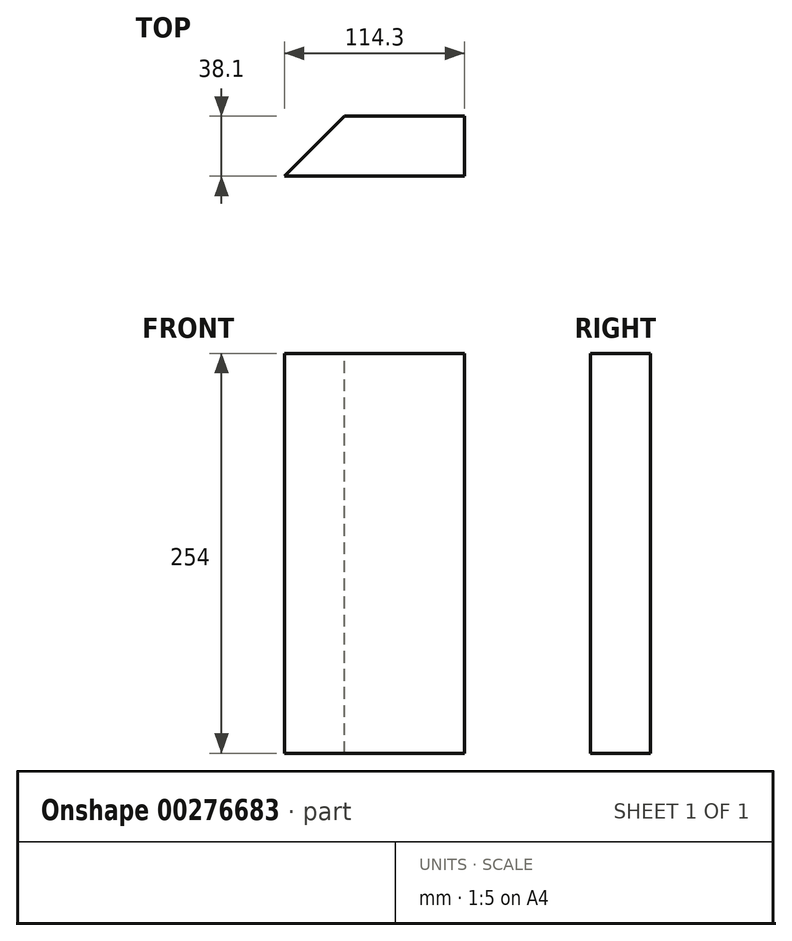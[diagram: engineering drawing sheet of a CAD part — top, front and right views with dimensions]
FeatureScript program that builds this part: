
annotation { "Feature Type Name" : "Feature", "Feature Type Description" : "" }
export const myFeature = defineFeature(function(context is Context, id is Id, definition is map)
    precondition{}
    {
        {
            var Q0;
            Q0=qCreatedBy(makeId("Top.planeOp"),FACE);
            var sketch = newSketch(context, id + "F0", { "sketchPlane" : qUnion([Q0])});
            skLineSegment(sketch, "E0.bottom", {"start": v(0, 0) * mm, "end": v(114.3, 0) * mm});
            skLineSegment(sketch, "E0.top", {"start": v(0, -38.1) * mm, "end": v(114.3, -38.1) * mm});
            skLineSegment(sketch, "E0.left", {"start": v(0, -38.1) * mm, "end": v(0, 0) * mm});
            skLineSegment(sketch, "E0.right", {"start": v(114.3, -38.1) * mm, "end": v(114.3, 0) * mm});
            skSolve(sketch);
        }
        {
            var Q0;
            Q0=qSketchRegion(id+"F0",true);
            extrude(context, id + "F1", {"entities" : qUnion([Q0]), "depth" : 254 * mm});
        }
        {
            var Q0;
            Q0=makeQuery(id+"F1.opExtrude","CAP_FACE",FACE,{"disambiguationData":[OSD([sQuery(id+"F0.wireOp",EDGE,"E0.bottom"),sQuery(id+"F0.wireOp",EDGE,"E0.top"),sQuery(id+"F0.wireOp",EDGE,"E0.left"),sQuery(id+"F0.wireOp",EDGE,"E0.right")])],"isStart":false});
            var sketch = newSketch(context, id + "F2", { "sketchPlane" : qUnion([Q0])});
            skLineSegment(sketch, "E1", {"start": v(0, -38.1) * mm, "end": v(38.1, 0) * mm});
            skSolve(sketch);
        }
        {
            var Q0;
            Q0 = qSketchRegion(id + "F2", true);
            var Q1;
            {var subQ0=sQuery(id+"F2.wireOp",EDGE,"E1");Q1=makeQuery(id+"F2.imprint","IMPRINT",FACE,{"disambiguationData":[TD([[makeQuery(id+"F2.imprint","IMPRINT",EDGE,{"derivedFrom":subQ0}),1.0]])]});}
            extrude(context, id + "F3", {"entities" : qUnion([Q0, Q1]), "operationType" : NewBodyOperationType.REMOVE, "oppositeDirection" : true, "depth" : 279.4 * mm});
        }
    });
